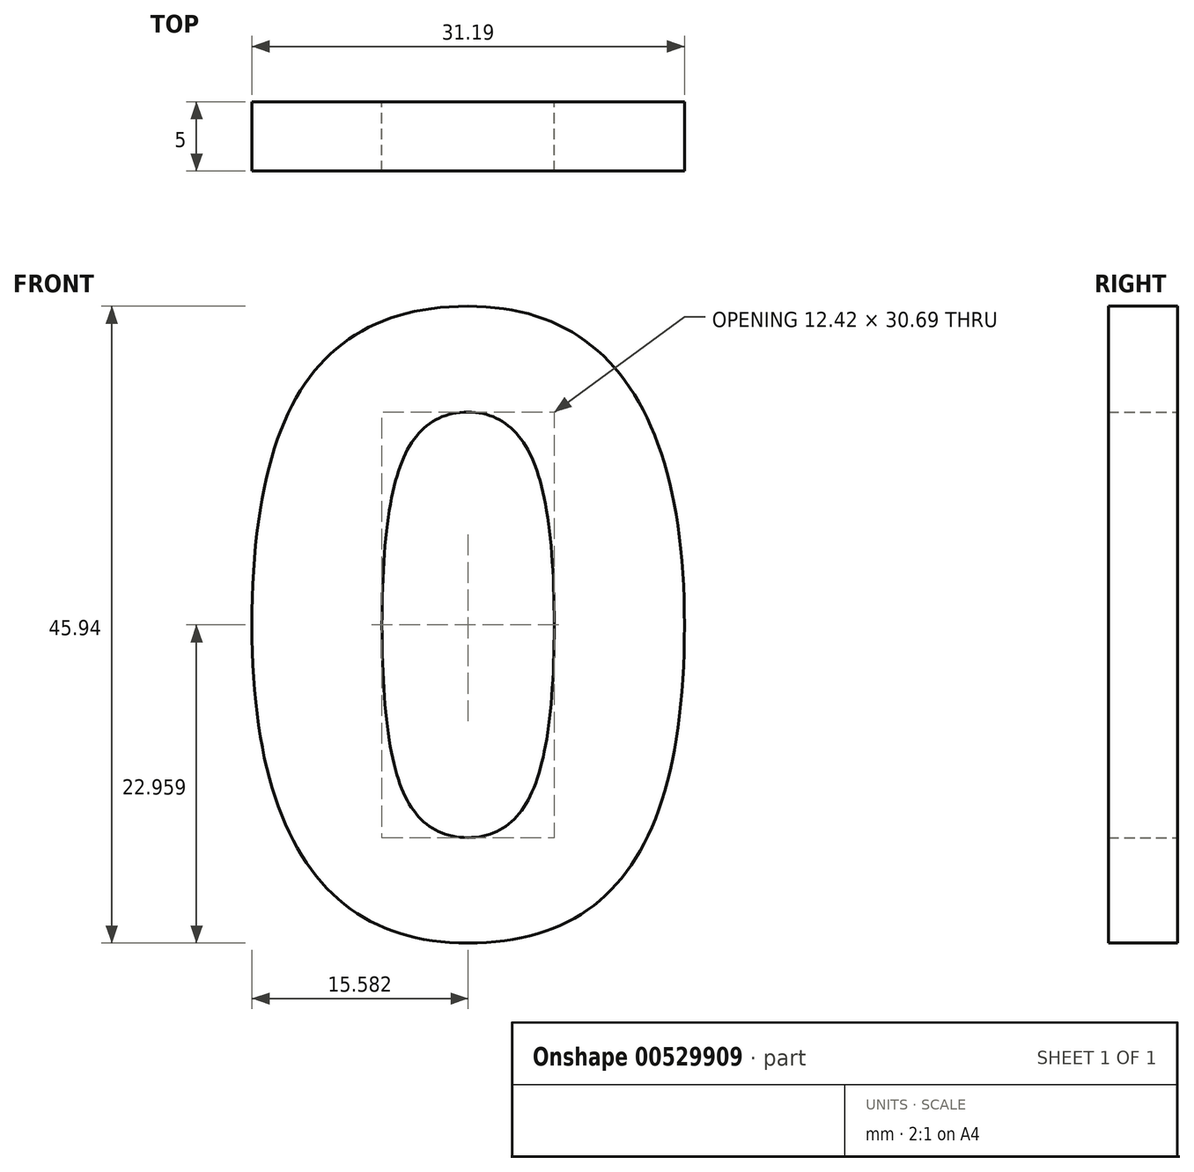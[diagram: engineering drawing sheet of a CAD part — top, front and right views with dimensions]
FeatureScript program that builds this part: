
annotation { "Feature Type Name" : "Feature", "Feature Type Description" : "" }
export const myFeature = defineFeature(function(context is Context, id is Id, definition is map)
    precondition{}
    {
        {
            var Q0;
            Q0=qCreatedBy(makeId("Front.planeOp"),FACE);
            var sketch = newSketch(context, id + "F0", { "sketchPlane" : qUnion([Q0])});
            skText(sketch, "E0", { "text": "0", "fontName": "OpenSans-Bold.ttf"});
            const initialGuessF0  = {"E0": [-0.05724, 0.00987, 1, 0, 0.045]};
            skSetInitialGuess(sketch, initialGuessF0);
            skSolve(sketch);
        }
        {
            var Q0;
            Q0=makeQuery(id+"F0.imprint","IMPRINT",FACE,{"disambiguationData":[TD([[makeQuery(id+"F0.imprint","IMPRINT",EDGE,{"derivedFrom":sQuery(id+"F0.wireOp",EDGE,"E0.sketch_text.stroke-0")}),-1.0]])]});
            extrude(context, id + "F1", {"entities" : qUnion([Q0]), "depth" : 5 * mm, "offsetDistance" : 25 * mm});
        }
    });
